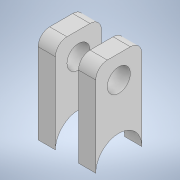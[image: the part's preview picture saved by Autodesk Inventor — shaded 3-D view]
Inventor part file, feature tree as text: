
AUTODESK INVENTOR PART (.ipt)
format: ipt  version: 2021 (Build 250183000, 183)  size: 130,560 bytes
history: native  units: in
note: dims shown in document units (in); Inventor stores cm internally (conversion verified against a paired STEP export)
features: extrude x2, sketch x2
ambient origin geometry x8: Origin, YZ Plane, XZ Plane, XY Plane, X Axis, Y Axis, Z Axis, Center Point
bodies: Solid1 (feature_tree)
feature tree (4):
  extrude  "Extrusion1"  Depth=0.5in
  extrude  "Extrusion3"  Depth=0.5in
  sketch  "Sketch1"  dims[d1=1.0in d2=0.5in]
  sketch  "Sketch3"  dims[d3=0.25in d5=0.5in d6=2.0in d7=1.5in d8=1.25in d9=0.0in d14=0.375in d15=0.5in d16=1.0in d17=0.0in]
